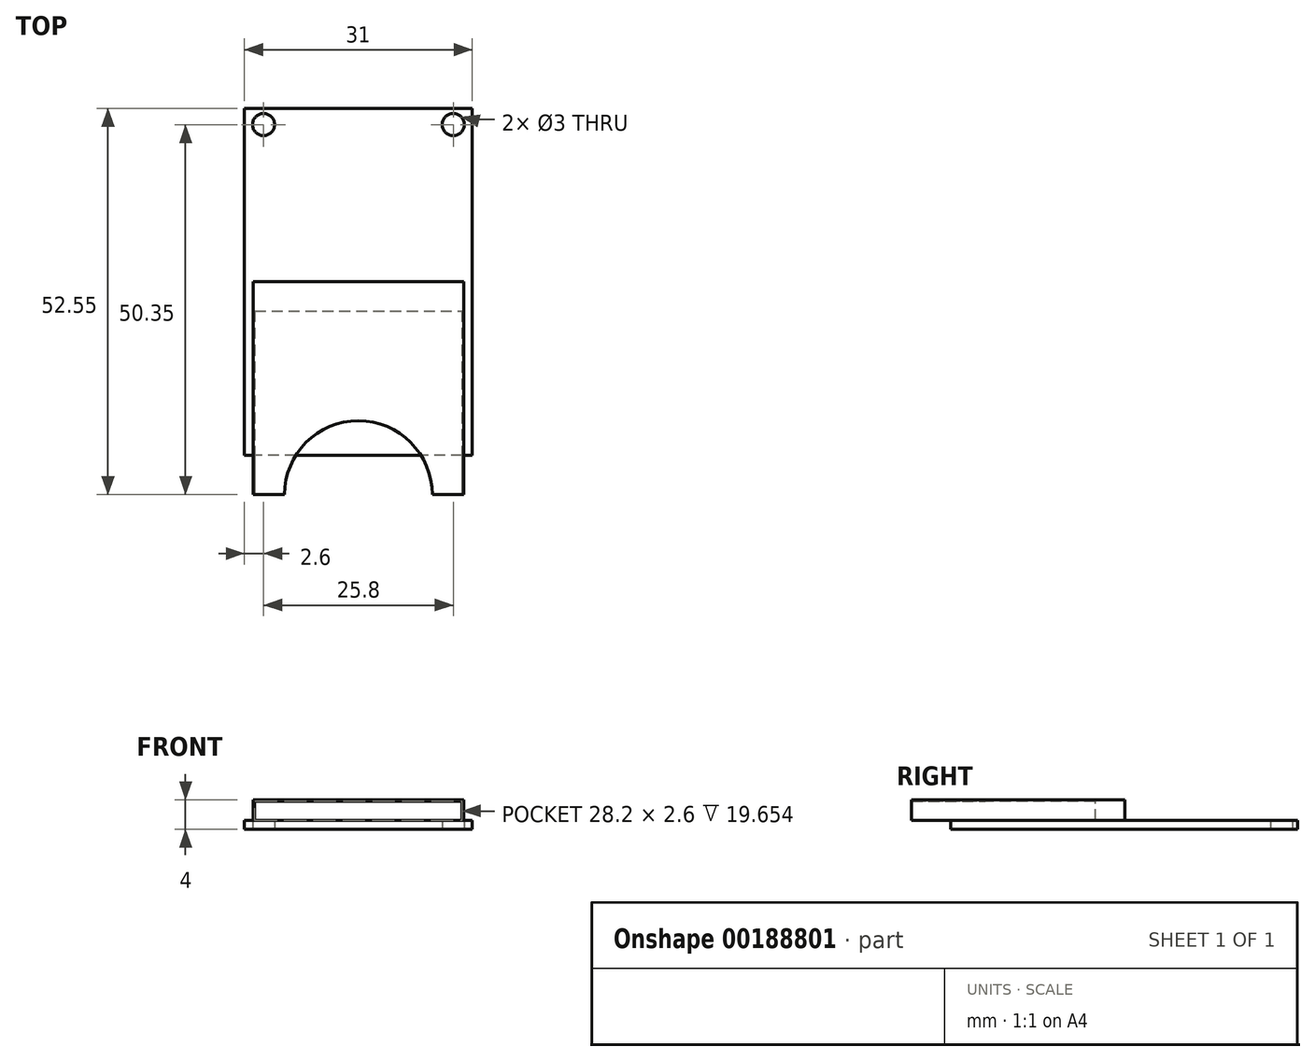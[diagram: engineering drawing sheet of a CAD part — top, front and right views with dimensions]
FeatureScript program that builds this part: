
annotation { "Feature Type Name" : "Feature", "Feature Type Description" : "" }
export const myFeature = defineFeature(function(context is Context, id is Id, definition is map)
    precondition{}
    {
        {
            var Q0;
            Q0=qCreatedBy(makeId("Top.planeOp"),FACE);
            var sketch = newSketch(context, id + "F0", { "sketchPlane" : qUnion([Q0])});
            skLineSegment(sketch, "E0.bottom", {"start": v(15.5, 23.6) * mm, "end": v(-15.5, 23.6) * mm});
            skLineSegment(sketch, "E0.top", {"start": v(15.5, -23.6) * mm, "end": v(-15.5, -23.6) * mm});
            skLineSegment(sketch, "E0.left", {"start": v(15.5, 23.6) * mm, "end": v(15.5, -23.6) * mm});
            skLineSegment(sketch, "E0.right", {"start": v(-15.5, 23.6) * mm, "end": v(-15.5, -23.6) * mm});
            skPoint(sketch, "E0.middle", {"position": v(0, 0) * mm});
            skCircle(sketch, "E1", {"center": v(-12.9, 21.4) * mm, "radius": 1.5 * mm});
            skCircle(sketch, "E2", {"center": v(12.9, 21.4) * mm, "radius": 1.5 * mm});
            skLineSegment(sketch, "E3", {"start": v(0, 23.6) * mm, "end": v(0, -23.6) * mm, "construction": true});
            skSolve(sketch);
        }
        {
            var Q0;
            Q0=makeQuery(id+"F0.imprint","IMPRINT",FACE,{"disambiguationData":[TD([[makeQuery(id+"F0.imprint","IMPRINT",EDGE,{"derivedFrom":sQuery(id+"F0.wireOp",EDGE,"E0.bottom")}),1.0]])]});
            extrude(context, id + "F1", {"entities" : qUnion([Q0]), "depth" : 1.2 * mm});
        }
        {
            var Q0;
            Q0=makeQuery(id+"F1.opExtrude","CAP_FACE",FACE,{"disambiguationData":[OSD([sQuery(id+"F0.wireOp",EDGE,"E0.bottom"),sQuery(id+"F0.wireOp",EDGE,"E0.top"),sQuery(id+"F0.wireOp",EDGE,"E0.left"),sQuery(id+"F0.wireOp",EDGE,"E0.right"),sQuery(id+"F0.wireOp",EDGE,"E1"),sQuery(id+"F0.wireOp",EDGE,"E2")])],"isStart":false});
            var sketch = newSketch(context, id + "F2", { "sketchPlane" : qUnion([Q0])});
            skLineSegment(sketch, "E4.bottom", {"start": v(14.3, -28.95) * mm, "end": v(-14.3, -28.95) * mm});
            skLineSegment(sketch, "E4.top", {"start": v(14.3, 0.05) * mm, "end": v(-14.3, 0.05) * mm});
            skLineSegment(sketch, "E4.left", {"start": v(14.3, -28.95) * mm, "end": v(14.3, 0.05) * mm});
            skLineSegment(sketch, "E4.right", {"start": v(-14.3, -28.95) * mm, "end": v(-14.3, 0.05) * mm});
            skPoint(sketch, "E4.middle", {"position": v(0, -14.45) * mm});
            skSolve(sketch);
        }
        {
            var Q0;
            Q0 = qSketchRegion(id + "F2", true);
            extrude(context, id + "F3", {"entities" : qUnion([Q0]), "operationType" : NewBodyOperationType.ADD, "depth" : 2.8 * mm});
        }
        {
            var Q0;
            Q0=makeQuery(id+"F3.opExtrude","SWEPT_FACE",FACE,{"disambiguationData":[OSD([sQuery(id+"F2.wireOp",EDGE,"E4.bottom")])]});
            var sketch = newSketch(context, id + "F4", { "sketchPlane" : qUnion([Q0])});
            skLineSegment(sketch, "E5.bottom", {"start": v(-14.1, 1.2) * mm, "end": v(14.1, 1.2) * mm});
            skLineSegment(sketch, "E5.top", {"start": v(-14.1, 3.8) * mm, "end": v(14.1, 3.8) * mm});
            skLineSegment(sketch, "E5.left", {"start": v(-14.1, 1.2) * mm, "end": v(-14.1, 3.8) * mm});
            skLineSegment(sketch, "E5.right", {"start": v(14.1, 1.2) * mm, "end": v(14.1, 3.8) * mm});
            skSolve(sketch);
        }
        {
            var Q0;
            Q0=makeQuery(id+"F4.imprint","IMPRINT",FACE,{"disambiguationData":[TD([[makeQuery(id+"F4.imprint","IMPRINT",EDGE,{"derivedFrom":sQuery(id+"F4.wireOp",EDGE,"E5.bottom")}),-1.0]])]});
            extrude(context, id + "F5", {"entities" : qUnion([Q0]), "operationType" : NewBodyOperationType.REMOVE, "oppositeDirection" : true, "depth" : 25 * mm});
        }
        {
            var Q0;
            Q0=makeQuery(id+"F3.opExtrude","CAP_FACE",FACE,{"disambiguationData":[OSD([sQuery(id+"F2.wireOp",EDGE,"E4.bottom"),sQuery(id+"F2.wireOp",EDGE,"E4.top"),sQuery(id+"F2.wireOp",EDGE,"E4.left"),sQuery(id+"F2.wireOp",EDGE,"E4.right")])],"isStart":false});
            var sketch = newSketch(context, id + "F6", { "sketchPlane" : qUnion([Q0])});
            skArc(sketch, "E6", {"start": v(10.05, -28.95) * mm, "mid": v(0, -18.9) * mm, "end": v(-10.05, -28.95) * mm});
            skLineSegment(sketch, "E7", {"start": v(0, 0) * mm, "end": v(0, -28.95) * mm, "construction": true});
            skSolve(sketch);
        }
        {
            var Q0;
            {var subQ0=sQuery(id+"F6.wireOp",EDGE,"E6");Q0=makeQuery(id+"F6.imprint","IMPRINT",FACE,{"disambiguationData":[TD([[makeQuery(id+"F6.imprint","IMPRINT",EDGE,{"derivedFrom":subQ0}),1.0]])]});}
            extrude(context, id + "F7", {"entities" : qUnion([Q0]), "operationType" : NewBodyOperationType.REMOVE, "endBound" : BoundingType.UP_TO_NEXT, "oppositeDirection" : true, "depth" : 25 * mm});
        }
    });
